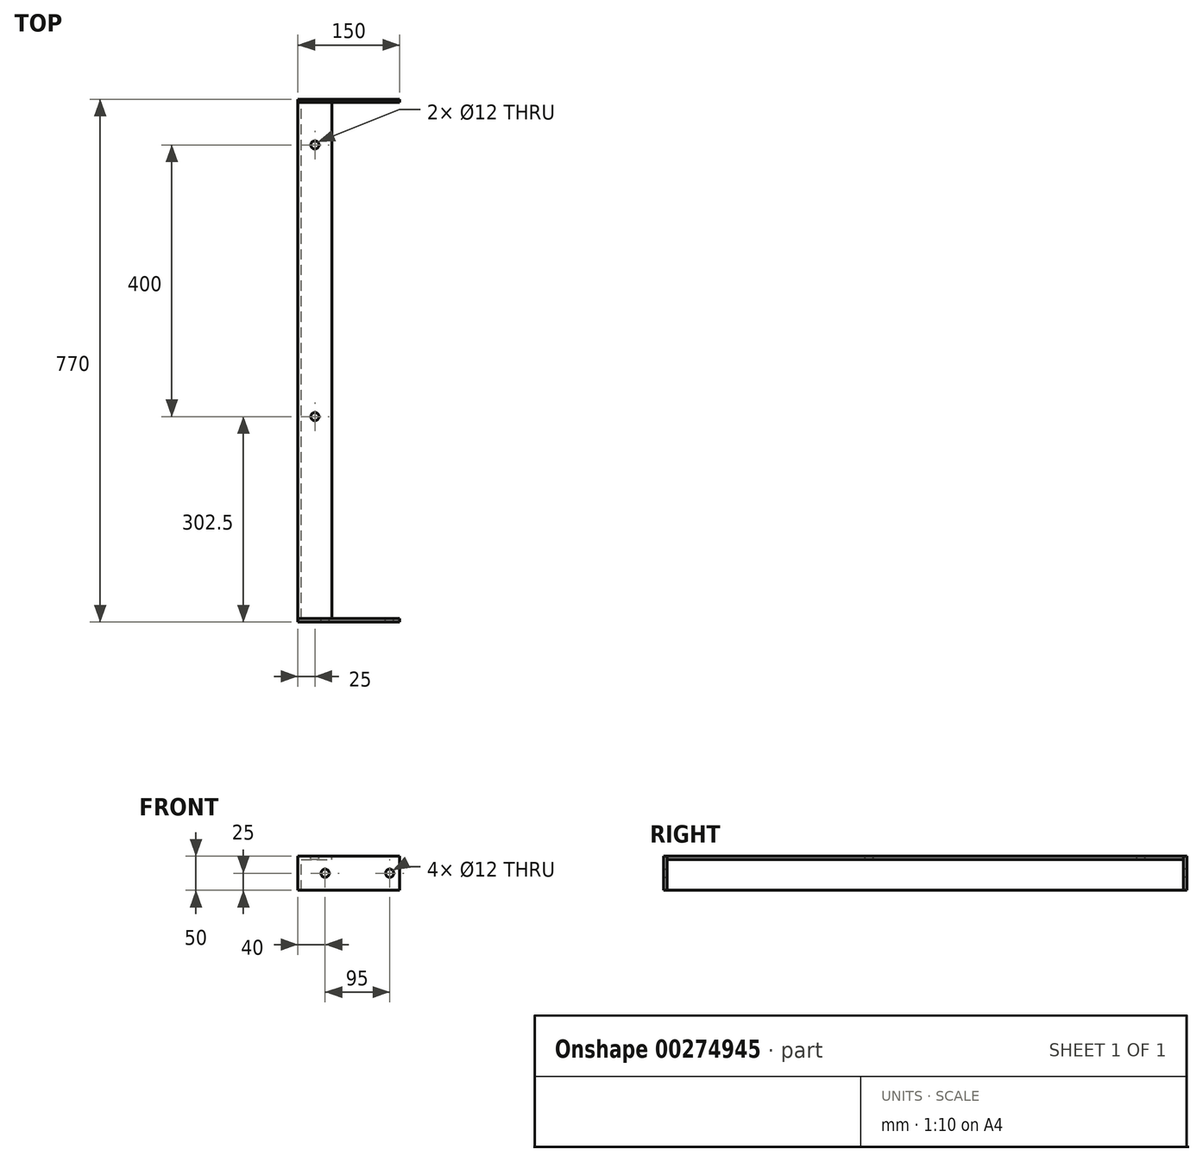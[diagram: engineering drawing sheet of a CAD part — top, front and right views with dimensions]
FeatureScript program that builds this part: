
annotation { "Feature Type Name" : "Feature", "Feature Type Description" : "" }
export const myFeature = defineFeature(function(context is Context, id is Id, definition is map)
    precondition{}
    {
        {
            var Q0;
            Q0=qCreatedBy(makeId("Front.planeOp"),FACE);
            var sketch = newSketch(context, id + "F0", { "sketchPlane" : qUnion([Q0])});
            skLineSegment(sketch, "E0", {"start": v(50, -5) * mm, "end": v(50, 0) * mm});
            skLineSegment(sketch, "E1", {"start": v(50, 0) * mm, "end": v(0, 0) * mm});
            skLineSegment(sketch, "E2", {"start": v(0, 0) * mm, "end": v(0, -50) * mm});
            skLineSegment(sketch, "E3", {"start": v(0, -50) * mm, "end": v(5, -50) * mm});
            skLineSegment(sketch, "E4", {"start": v(5, -50) * mm, "end": v(5, -5) * mm});
            skLineSegment(sketch, "E5", {"start": v(5, -5) * mm, "end": v(50, -5) * mm});
            skSolve(sketch);
        }
        {
            var Q0;
            Q0=makeQuery(id+"F0.imprint","IMPRINT",FACE,{"disambiguationData":[TD([[makeQuery(id+"F0.imprint","IMPRINT",EDGE,{"derivedFrom":sQuery(id+"F0.wireOp",EDGE,"E0")}),1.0]])]});
            extrude(context, id + "F1", {"entities" : qUnion([Q0]), "depth" : 760 * mm, "symmetric" : true});
        }
        {
            var Q0;
            Q0=makeQuery(id+"F1.opExtrude","CAP_FACE",FACE,{"disambiguationData":[OSD([sQuery(id+"F0.wireOp",EDGE,"E0"),sQuery(id+"F0.wireOp",EDGE,"E1"),sQuery(id+"F0.wireOp",EDGE,"E2"),sQuery(id+"F0.wireOp",EDGE,"E3"),sQuery(id+"F0.wireOp",EDGE,"E4"),sQuery(id+"F0.wireOp",EDGE,"E5")])],"isStart":true});
            var sketch = newSketch(context, id + "F2", { "sketchPlane" : qUnion([Q0])});
            skLineSegment(sketch, "E6.bottom", {"start": v(-150, 0) * mm, "end": v(0, 0) * mm});
            skLineSegment(sketch, "E6.top", {"start": v(-150, -50) * mm, "end": v(0, -50) * mm});
            skLineSegment(sketch, "E6.left", {"start": v(-150, 0) * mm, "end": v(-150, -50) * mm});
            skLineSegment(sketch, "E6.right", {"start": v(0, 0) * mm, "end": v(0, -50) * mm});
            skLineSegment(sketch, "E7", {"start": v(-150, -25) * mm, "end": v(-135, -25) * mm, "construction": true});
            skCircle(sketch, "E8", {"center": v(-135, -25) * mm, "radius": 6 * mm});
            skCircle(sketch, "E9", {"center": v(-40, -25) * mm, "radius": 6 * mm});
            skLineSegment(sketch, "E10.trimOffspring", {"start": v(-40, -25) * mm, "end": v(0, -25) * mm, "construction": true});
            skSolve(sketch);
        }
        {
            var Q0;
            {var subQ0=sQuery(id+"F2.wireOp",EDGE,"E6.left");Q0=makeQuery(id+"F2.imprint","IMPRINT",FACE,{"disambiguationData":[TD([[makeQuery(id+"F2.imprint","IMPRINT",EDGE,{"derivedFrom":subQ0}),1.0]])]});}
            var Q1;
            {var subQ3=makeQuery(id+"F1.opExtrude","CAP_EDGE",EDGE,{"disambiguationData":[OSD([sQuery(id+"F0.wireOp",EDGE,"E0")])],"isStart":true});Q1=makeQuery(id+"F2.imprint","IMPRINT",FACE,{"disambiguationData":[TD([[makeQuery(id+"F2.imprint","IMPRINT",EDGE,{"derivedFrom":subQ3}),-1.0]])]});}
            var Q2;
            {var subQ0=sQuery(id+"F2.wireOp",EDGE,"E6.right");Q2=makeQuery(id+"F2.imprint","IMPRINT",FACE,{"disambiguationData":[TD([[makeQuery(id+"F2.imprint","IMPRINT",EDGE,{"derivedFrom":subQ0}),-1.0]])]});}
            extrude(context, id + "F3", {"entities" : qUnion([Q0, Q1, Q2]), "depth" : 5 * mm});
        }
        {
            var Q0;
            Q0=makeQuery(id+"F3.opExtrude","SWEPT_BODY",BODY,{"disambiguationData":[OSD([sQuery(id+"F2.wireOp",EDGE,"E6.bottom"),sQuery(id+"F2.wireOp",EDGE,"E6.top"),sQuery(id+"F2.wireOp",EDGE,"E6.left"),sQuery(id+"F2.wireOp",EDGE,"E6.right"),sQuery(id+"F2.wireOp",EDGE,"E8"),sQuery(id+"F2.wireOp",EDGE,"E9")])]});
            var Q1;
            Q1=qCreatedBy(makeId("Front.planeOp"),FACE);
            mirror(context, id + "F4", {"entities" : qUnion([Q0]), "mirrorPlane" : qUnion([Q1])});
        }
        {
            var Q0;
            Q0=makeQuery(id+"F1.opExtrude","SWEPT_FACE",FACE,{"disambiguationData":[OSD([sQuery(id+"F0.wireOp",EDGE,"E1")])]});
            var sketch = newSketch(context, id + "F5", { "sketchPlane" : qUnion([Q0])});
            skLineSegment(sketch, "E11", {"start": v(0, 0) * mm, "end": v(50, 0) * mm, "construction": true});
            skLineSegment(sketch, "E12", {"start": v(25, 317.5) * mm, "end": v(25, -82.5) * mm, "construction": true});
            skCircle(sketch, "E13", {"center": v(25, 317.5) * mm, "radius": 6 * mm});
            skCircle(sketch, "E14", {"center": v(25, -82.5) * mm, "radius": 6 * mm});
            skSolve(sketch);
        }
        {
            var Q0;
            Q0=makeQuery(id+"F5.imprint","IMPRINT",FACE,{"disambiguationData":[TD([[makeQuery(id+"F5.imprint","IMPRINT",EDGE,{"derivedFrom":sQuery(id+"F5.wireOp",EDGE,"E13")}),1.0]])]});
            var Q1;
            Q1=makeQuery(id+"F5.imprint","IMPRINT",FACE,{"disambiguationData":[TD([[makeQuery(id+"F5.imprint","IMPRINT",EDGE,{"derivedFrom":sQuery(id+"F5.wireOp",EDGE,"E14")}),1.0]])]});
            extrude(context, id + "F6", {"entities" : qUnion([Q0, Q1]), "operationType" : NewBodyOperationType.REMOVE, "endBound" : BoundingType.THROUGH_ALL, "oppositeDirection" : true, "depth" : 25 * mm});
        }
    });
